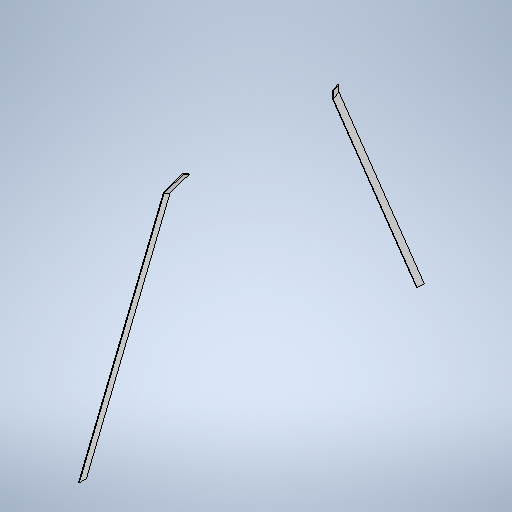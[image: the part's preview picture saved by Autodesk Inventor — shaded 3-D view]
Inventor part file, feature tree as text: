
AUTODESK INVENTOR PART (.ipt)
format: ipt  version: 2025.3 (Build 293356030, 356C)  size: 271,360 bytes
history: native  units: mm
features: sketch x3, sweep x2, plane x1
ambient origin geometry x8: Origin, YZ Plane, XZ Plane, XY Plane, X Axis, Y Axis, Z Axis, Center Point
bodies: Body1 (feature_tree)
feature tree (6):
  sketch  "3D Sketch2"
  plane  "Work Plane2"
  sweep  "Sweep3"
  sweep  "Sweep4"
  sketch  "Sketch4"  dims[d7=1100.0mm d8=1100.0mm]
  sketch  "Sketch5"  dims[d9=2200.0mm d10=2200.0mm d11=6.981317mm d14=10.0mm d15=100.0mm d16=0.0mm d17=0.0mm d18=10.0mm d19=100.0mm d20=0.0mm d21=0.0mm d22=300.0mm]
